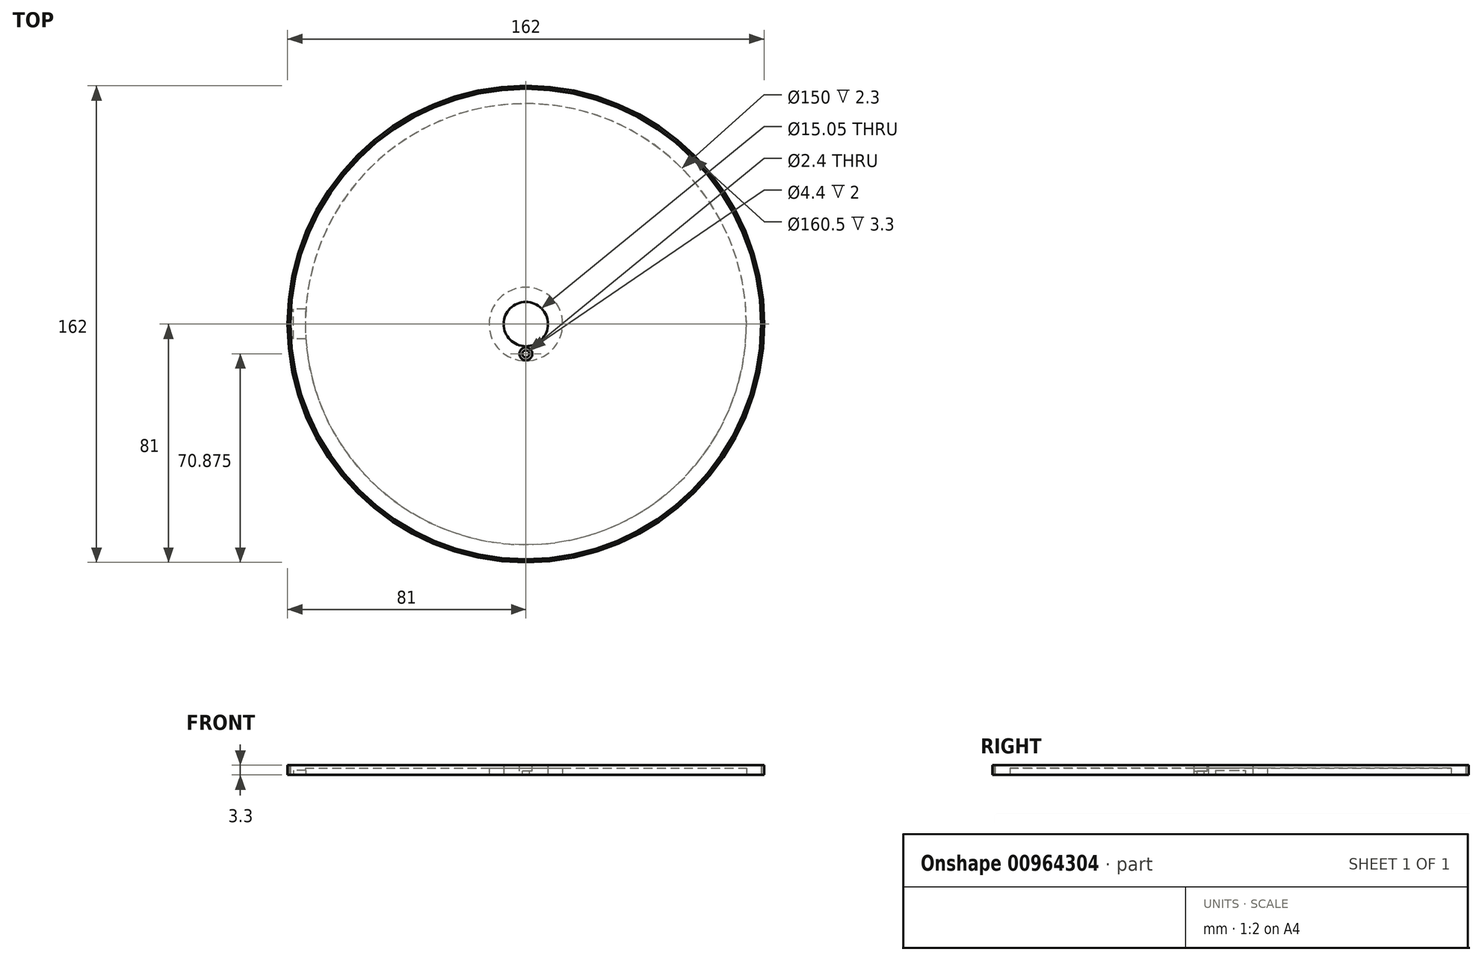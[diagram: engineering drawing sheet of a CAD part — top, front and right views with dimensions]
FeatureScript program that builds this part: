
annotation { "Feature Type Name" : "Feature", "Feature Type Description" : "" }
export const myFeature = defineFeature(function(context is Context, id is Id, definition is map)
    precondition{}
    {
        {
            var Q0;
            Q0=qCreatedBy(makeId("Top.planeOp"),FACE);
            var sketch = newSketch(context, id + "F0", { "sketchPlane" : qUnion([Q0])});
            skCircle(sketch, "E0", {"center": v(0, 0) * mm, "radius": 80 * mm});
            skSolve(sketch);
        }
        {
            var Q0;
            Q0 = qSketchRegion(id + "F0", true);
            extrude(context, id + "F1", {"entities" : qUnion([Q0]), "depth" : 3.3 * mm, "offsetDistance" : 25 * mm});
        }
        {
            var Q0;
            Q0=makeQuery(id+"F1.opExtrude","CAP_FACE",FACE,{"disambiguationData":[OSD([sQuery(id+"F0.wireOp",EDGE,"E0")])],"isStart":true});
            var sketch = newSketch(context, id + "F2", { "sketchPlane" : qUnion([Q0])});
            skCircle(sketch, "E1", {"center": v(0, 0) * mm, "radius": 7.53 * mm});
            skSolve(sketch);
        }
        {
            var Q0;
            Q0 = qSketchRegion(id + "F2", true);
            extrude(context, id + "F3", {"entities" : qUnion([Q0]), "operationType" : NewBodyOperationType.REMOVE, "endBound" : BoundingType.THROUGH_ALL, "oppositeDirection" : true, "depth" : 25 * mm, "offsetDistance" : 25 * mm});
        }
        {
            var Q0;
            Q0=makeQuery(id+"F1.opExtrude","CAP_FACE",FACE,{"disambiguationData":[OSD([sQuery(id+"F0.wireOp",EDGE,"E0")])],"isStart":true});
            var sketch = newSketch(context, id + "F4", { "sketchPlane" : qUnion([Q0])});
            skCircle(sketch, "E2", {"center": v(0, 0) * mm, "radius": 12.5 * mm});
            skCircle(sketch, "E3", {"center": v(0, 0) * mm, "radius": 75 * mm});
            skSolve(sketch);
        }
        {
            var Q0;
            Q0 = qSketchRegion(id + "F4", true);
            extrude(context, id + "F5", {"entities" : qUnion([Q0]), "operationType" : NewBodyOperationType.REMOVE, "oppositeDirection" : true, "depth" : 2.3 * mm, "offsetDistance" : 25 * mm});
        }
        {
            var Q0;
            Q0=makeQuery(id+"F1.opExtrude","CAP_FACE",FACE,{"disambiguationData":[OSD([sQuery(id+"F0.wireOp",EDGE,"E0")])],"isStart":false});
            var sketch = newSketch(context, id + "F6", { "sketchPlane" : qUnion([Q0])});
            skLineSegment(sketch, "E4", {"start": v(0, -7.53) * mm, "end": v(0, -10.12) * mm});
            skSolve(sketch);
        }
        {
            var Q0;
            Q0=sQuery(id+"F6.wireOp",VERTEX,"E4.end");
            var Q1;
            Q1=makeQuery(id+"F1.opExtrude","SWEPT_BODY",BODY,{"disambiguationData":[OSD([sQuery(id+"F0.wireOp",EDGE,"E0")])]});
            hole(context, id + "F7", {"style" : HoleStyle.C_BORE, "endStyle" : HoleEndStyle.THROUGH, "standardTappedOrClearance" : lookupTablePath({ "fit" : "Normal", "standard" : "ISO", "size" : "M2", "type" : "Clearance" }), "standardBlindInLast" : lookupTablePath({ "fit" : "Normal", "standard" : "ISO", "engagement" : "75%", "pitch" : "0.25 mm", "size" : "M2", "type" : "Clearance & tapped" }), "holeDiameter" : 2.4 * mm, "cBoreDiameter" : 4.4 * mm, "cBoreDepth" : 2 * mm, "majorDiameter" : 5 * mm, "tappedDepth" : 12 * mm, "tapClearance" : 3, "startFromSketch" : true, "locations" : qUnion([Q0]), "scope" : qUnion([Q1])});
        }
        {
            var Q0;
            {var subQ0=sQuery(id+"F0.wireOp",EDGE,"E0");Q0=makeQuery(id+"F5.boolean.opBoolean","SPLIT",FACE,{"disambiguationData":[TD([makeQuery(id+"F1.opExtrude","SWEPT_FACE",FACE,{"disambiguationData":[OSD([subQ0])]})])],"derivedFrom":makeQuery(id+"F1.opExtrude","CAP_FACE",FACE,{"disambiguationData":[OSD([subQ0])],"isStart":true})});}
            var sketch = newSketch(context, id + "F8", { "sketchPlane" : qUnion([Q0])});
            skLineSegment(sketch, "E5.bottom", {"start": v(-74.83, 5.08) * mm, "end": v(-78.98, 5.08) * mm});
            skLineSegment(sketch, "E5.top", {"start": v(-74.83, -5.07) * mm, "end": v(-78.98, -5.07) * mm});
            skLineSegment(sketch, "E5.left", {"start": v(-74.83, 5.08) * mm, "end": v(-74.83, -5.07) * mm});
            skLineSegment(sketch, "E5.right", {"start": v(-78.98, 5.08) * mm, "end": v(-78.98, -5.07) * mm});
            skPoint(sketch, "E5.middle", {"position": v(-76.9, 0) * mm});
            skSolve(sketch);
        }
        {
            var Q0;
            Q0 = qSketchRegion(id + "F8", true);
            extrude(context, id + "F9", {"entities" : qUnion([Q0]), "operationType" : NewBodyOperationType.REMOVE, "oppositeDirection" : true, "depth" : 1.51 * mm, "offsetDistance" : 25 * mm});
        }
        {
            var Q0;
            Q0=makeQuery(id+"F1.opExtrude","CAP_FACE",FACE,{"disambiguationData":[OSD([sQuery(id+"F0.wireOp",EDGE,"E0")])],"isStart":false});
            var sketch = newSketch(context, id + "F10", { "sketchPlane" : qUnion([Q0])});
            skCircle(sketch, "E6", {"center": v(0, 0) * mm, "radius": 81 * mm});
            skCircle(sketch, "E7", {"center": v(0, 0) * mm, "radius": 80.25 * mm});
            skSolve(sketch);
        }
        {
            var Q0;
            Q0 = qSketchRegion(id + "F10", true);
            extrude(context, id + "F11", {"entities" : qUnion([Q0]), "oppositeDirection" : true, "depth" : 3.3 * mm, "offsetDistance" : 25 * mm});
        }
    });
